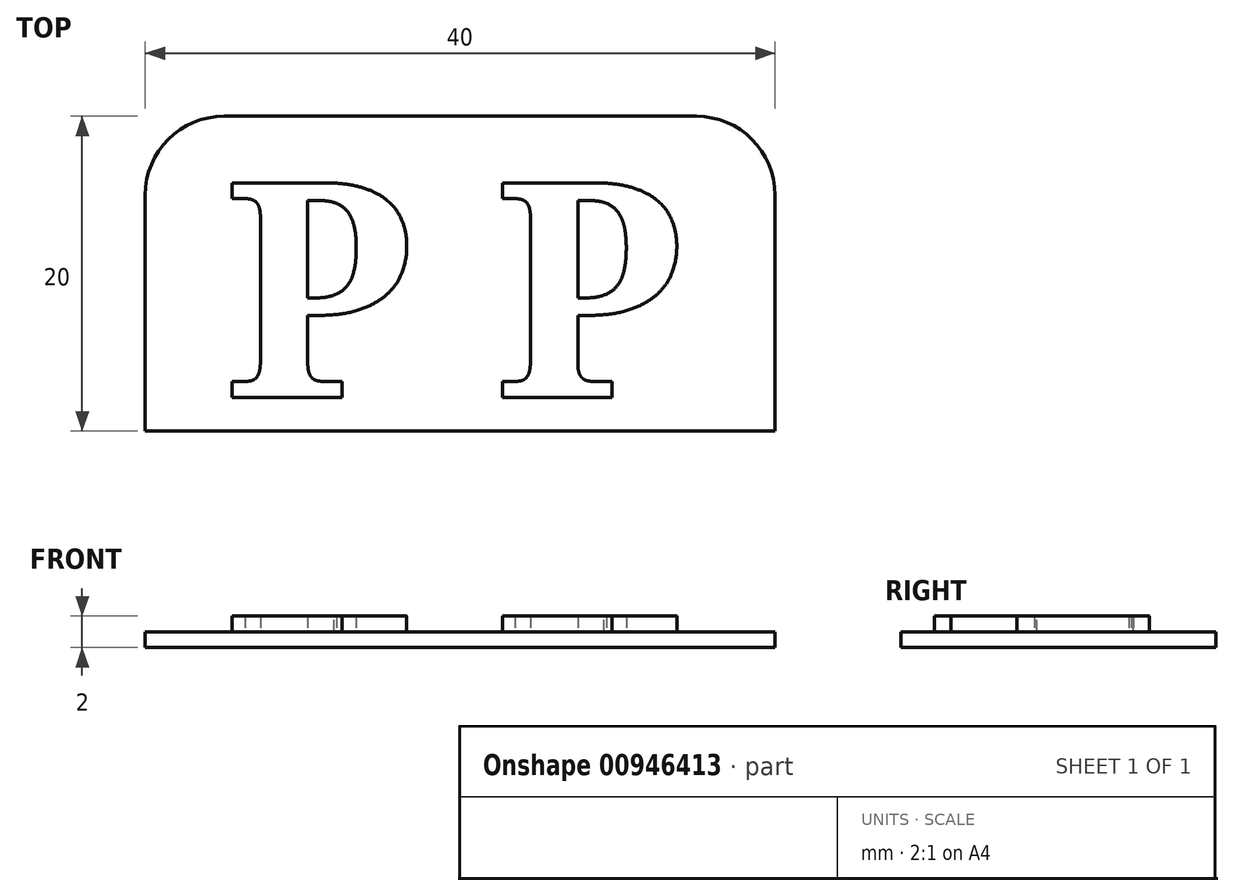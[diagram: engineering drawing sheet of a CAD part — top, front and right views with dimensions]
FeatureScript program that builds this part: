
annotation { "Feature Type Name" : "Feature", "Feature Type Description" : "" }
export const myFeature = defineFeature(function(context is Context, id is Id, definition is map)
    precondition{}
    {
        {
            var Q0;
            Q0=qCreatedBy(makeId("Top.planeOp"),FACE);
            var sketch = newSketch(context, id + "F0", { "sketchPlane" : qUnion([Q0])});
            skLineSegment(sketch, "E0.bottom", {"start": v(-20, 10) * mm, "end": v(20, 10) * mm});
            skLineSegment(sketch, "E0.top", {"start": v(-20, -10) * mm, "end": v(20, -10) * mm});
            skLineSegment(sketch, "E0.left", {"start": v(-20, 10) * mm, "end": v(-20, -10) * mm});
            skLineSegment(sketch, "E0.right", {"start": v(20, 10) * mm, "end": v(20, -10) * mm});
            skPoint(sketch, "E0.middle", {"position": v(0, 0) * mm});
            skSolve(sketch);
        }
        {
            var Q0;
            Q0=makeQuery(id+"F0.imprint","IMPRINT",FACE,{"disambiguationData":[TD([[makeQuery(id+"F0.imprint","IMPRINT",EDGE,{"derivedFrom":sQuery(id+"F0.wireOp",EDGE,"E0.bottom")}),-1.0]])]});
            extrude(context, id + "F1", {"entities" : qUnion([Q0]), "depth" : 1 * mm, "offsetDistance" : 25 * mm});
        }
        {
            var Q0;
            Q0=makeQuery(id+"F1.opExtrude","CAP_FACE",FACE,{"disambiguationData":[OSD([sQuery(id+"F0.wireOp",EDGE,"E0.bottom"),sQuery(id+"F0.wireOp",EDGE,"E0.top"),sQuery(id+"F0.wireOp",EDGE,"E0.left"),sQuery(id+"F0.wireOp",EDGE,"E0.right")])],"isStart":false});
            var sketch = newSketch(context, id + "F2", { "sketchPlane" : qUnion([Q0])});
            skText(sketch, "E1", { "text": "P P", "fontName": "NotoSerif-Bold.ttf"});
            const initialGuessF2  = {"E1": [-0.015, -0.00786, 1, 0, 0.01375]};
            skSetInitialGuess(sketch, initialGuessF2);
            skSolve(sketch);
        }
        {
            var Q0;
            Q0=qSketchRegion(id+"F2",true);
            extrude(context, id + "F3", {"entities" : qUnion([Q0]), "operationType" : NewBodyOperationType.ADD, "depth" : 1 * mm, "offsetDistance" : 25 * mm});
        }
        {
            var Q0;
            Q0=makeQuery(id+"F1.opExtrude","SWEPT_EDGE",EDGE,{"disambiguationData":[OSD([sQuery(id+"F0.wireOp",EDGE,"E0.bottom"),sQuery(id+"F0.wireOp",EDGE,"E0.left")])]});
            var Q1;
            Q1=makeQuery(id+"F1.opExtrude","SWEPT_EDGE",EDGE,{"disambiguationData":[OSD([sQuery(id+"F0.wireOp",EDGE,"E0.bottom"),sQuery(id+"F0.wireOp",EDGE,"E0.right")])]});
            fillet(context, id + "F4", {"entities" : qUnion([Q0, Q1]), "radius" : 5 * mm, "tangentPropagation" : true, "allowEdgeOverflow" : false});
        }
    });
